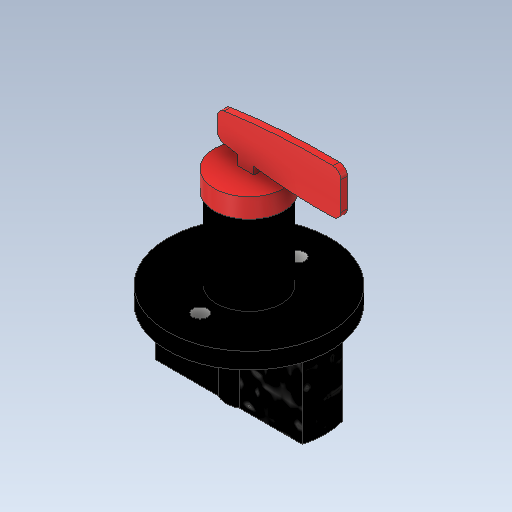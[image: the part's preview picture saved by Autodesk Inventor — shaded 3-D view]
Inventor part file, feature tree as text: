
AUTODESK INVENTOR PART (.ipt)
format: ipt  version: 2021 (Build 250183000, 183)  size: 189,440 bytes
history: native  units: in
note: dims shown in document units (in); Inventor stores cm internally (conversion verified against a paired STEP export)
features: extrude x8, sketch x8
ambient origin geometry x8: Origin, YZ Plane, XZ Plane, XY Plane, X Axis, Y Axis, Z Axis, Center Point
bodies: Solid1 (feature_tree)
feature tree (16):
  extrude  "Extrusion1"  Depth=0.25in TaperAngle=0.0deg
  extrude  "Extrusion3"  Depth=1.25in TaperAngle=0.0deg
  extrude  "Extrusion4"  Depth=0.25in
  extrude  "Extrusion5"  Depth=0.1in TaperAngle=0.0deg
  extrude  "Extrusion6"  Depth=0.125in
  extrude  "Extrusion7"  Depth=0.1in TaperAngle=0.0deg
  extrude  "Extrusion8"  Depth=1.156in TaperAngle=0.0deg
  extrude  "Extrusion9"  Depth=0.502in
  sketch  "Sketch1"  dims[d0=2.5in d1=0.25in d2=0.0in]
  sketch  "Sketch3"  dims[d9=1.0in d10=1.25in d11=0.0in]
  sketch  "Sketch4"  dims[d12=0.3in d13=0.0in d14=0.25in]
  sketch  "Sketch5"  dims[d15=0.1in d16=0.1in d17=0.0in]
  sketch  "Sketch6"  dims[d18=0.125in d19=0.125in]
  sketch  "Sketch7"  dims[d20=0.1in d21=0.0in d22=1.0in d23=0.0in]
  sketch  "Sketch8"  dims[d24=0.7in d25=1.156in d26=0.0in]
  sketch  "Sketch10"  dims[d31=0.502in d32=0.502in d33=0.23in d34=1.0in d35=0.0in]
